# Revit family: TapSet_Basin_Nero_Kara_Wall
name_source: partatom
category: Plumbing Fixtures
units: mm (PartAtom-declared; Revit-internal decimal feet)

## family parameters
Always vertical = Yes
Cut with Voids When Loaded = Yes
Maintain Annotation Orientation = No
OmniClass Number = 23.31.11.19
OmniClass Title = Faucet Mixing Valves
Part Type = Normal
Room Calculation Point = No
Round Connector Dimension = Use Diameter
Shared = No
Work Plane-Based = No

## types (12) — shared parameters
Assembly Code = C1030210
CW Connection = Yes
HW Connection = Yes
IfcExportAs = ifcValve
IfcExportType = FAUCET
Manufacturer = Nero
ManufacturerOverallHeight = 73.75 mm  [stored 0.241962 ft]
ManufacturerOverallWidth = 309.5 mm  [stored 1.01542 ft]
ManufacturerURLProductSpecific = https://nerotapware.com.au
ModifiedIssue = 20231106 $
URL = https://nerotapware.com.au
Uniclass2015Code = Pr_40_20_87_55
Uniclass2015Title = Mixer taps
Uniclass2015Version = Products v1.28
Vent Connection = No
Waste Connection = No
zero-valued in all types: Default Elevation

## per-type parameters (varying)
| type | BodyMaterial | Description | ManufacturerOverallDepth | ManufacturerSpecCode | Model | Type Comments |
| Matte Black (NR211707A217MB) | Metal_MatteBlack_Nero | Kara Wall Basin Set Matte Black | 226 mm  [stored 0.74147 ft] | NR211707A217MB | NR211707A217MB | Tap Set - Basin - Wall - Matte Black |
| Gun Metal (NR211707a217GM) | Metal_GunMetal_Nero | Kara Wall Basin Set Gun Metal Grey | 226 mm  [stored 0.74147 ft] | NR211707a217GM | NR211707a217GM | Tap Set - Basin - Wall - Gun Metal |
| Chrome (NR211707a217CH) | Metal_Chrome_Nero | Kara Wall Basin Set Chrome | 226 mm  [stored 0.74147 ft] | NR211707a217CH | NR211707a217CH | Tap Set - Basin - Wall - Chrome |
| Brushed Bronze (NR211707A217BZ) | Metal_Bronze_Nero_Brushed | Kara Wall Basin Set Bronze | 226 mm  [stored 0.74147 ft] | NR211707A217BZ | NR211707A217BZ | Tap Set - Basin - Wall - Brushed Bronze |
| Brushed Nickel (NR211707a217BN) | Metal_Nickel_Nero_Brushed | Kara Wall Basin Set Brushed Nickel | 226 mm  [stored 0.74147 ft] | NR211707a217BN | NR211707a217BN | Tap Set - Basin - Wall - Brushed Nickel |
| Brushed Gold (NR211707a217BG) | Metal_Gold_Nero_Brushed | Kara Wall Basin Set Brushed Gold | 226 mm  [stored 0.74147 ft] | NR211707a217BG | NR211707a217BG | Tap Set - Basin - Wall - Brushed Gold |
| Matte Black (NR211707A180MB) | Metal_MatteBlack_Nero | Kara Wall Basin Set Matte Black | 192 mm | NR211707A180MB | NR211707A180MB | Tap Set - Basin - Wall - Matte Black |
| Gun Metal (NR211707a180GM) | Metal_GunMetal_Nero | Kara Wall Basin Set Gun Metal Grey | 192 mm | NR211707a180GM | NR211707a180GM | Tap Set - Basin - Wall - Gun Metal |
| Chrome (NR211707a180CH) | Metal_Chrome_Nero | Kara Wall Basin Set Chrome | 192 mm | NR211707a180CH | NR211707a180CH | Tap Set - Basin - Wall - Chrome |
| Brushed Bronze (NR211707A180BZ) | Metal_Bronze_Nero_Brushed | Kara Wall Basin Set Bronze | 192 mm | NR211707A180BZ | NR211707A180BZ | Tap Set - Basin - Wall - Brushed Bronze |
| Brushed Nickel (NR211707a180BN) | Metal_Nickel_Nero_Brushed | Kara Wall Basin Set Brushed Nickel | 192 mm | NR211707a180BN | NR211707a180BN | Tap Set - Basin - Wall - Brushed Nickel |
| Brushed Gold (NR211707a180BG) | Metal_Gold_Nero_Brushed | Kara Wall Basin Set Brushed Gold | 192 mm | NR211707a180BG | NR211707a180BG | Tap Set - Basin - Wall - Brushed Gold |

note: [stored X ft] marks values corroborated as IEEE doubles in the binary element streams (Revit-internal decimal feet)

## geometry (parser evidence)
native form markers: Sweep x2
no freeform markers — native parametric forms only
